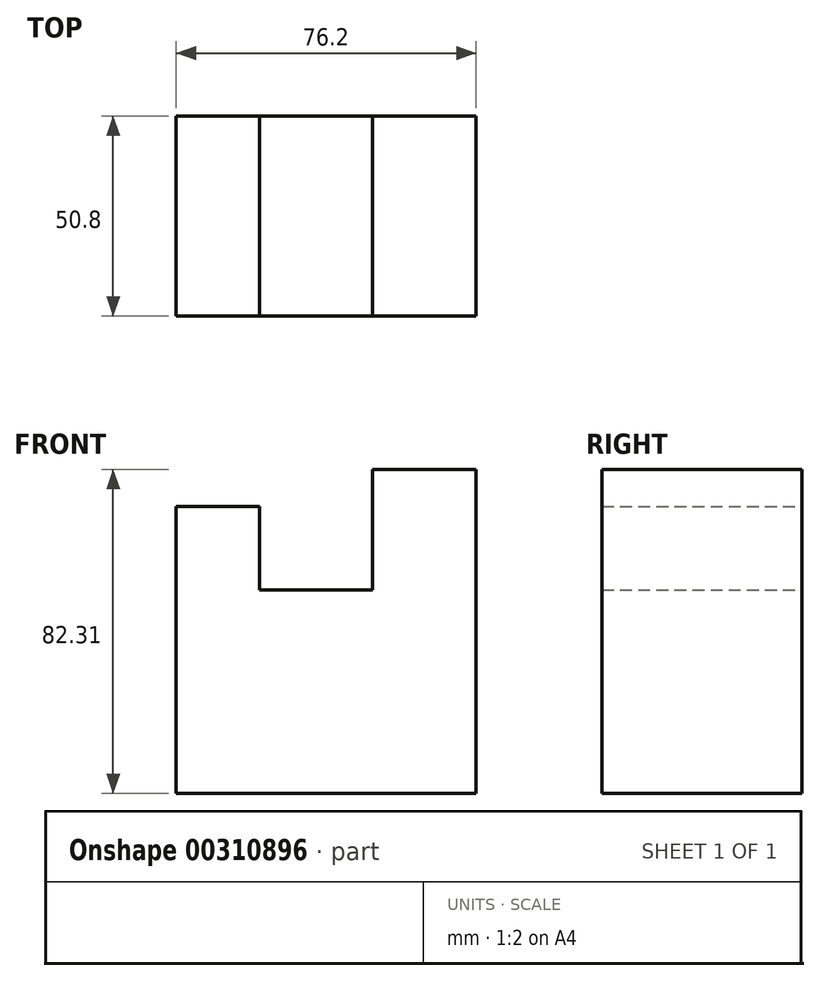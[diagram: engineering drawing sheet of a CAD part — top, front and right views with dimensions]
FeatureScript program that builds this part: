
annotation { "Feature Type Name" : "Feature", "Feature Type Description" : "" }
export const myFeature = defineFeature(function(context is Context, id is Id, definition is map)
    precondition{}
    {
        {
            var Q0;
            Q0=qCreatedBy(makeId("Front.planeOp"),FACE);
            var sketch = newSketch(context, id + "F0", { "sketchPlane" : qUnion([Q0])});
            skLineSegment(sketch, "E0", {"start": v(-55.43, -57.56) * mm, "end": v(20.77, -57.56) * mm});
            skLineSegment(sketch, "E1", {"start": v(20.77, -57.56) * mm, "end": v(20.77, 24.75) * mm});
            skLineSegment(sketch, "E2", {"start": v(-5.57, 24.75) * mm, "end": v(20.77, 24.75) * mm});
            skLineSegment(sketch, "E3", {"start": v(-5.57, 24.75) * mm, "end": v(-5.57, -5.82) * mm});
            skLineSegment(sketch, "E4", {"start": v(-34.27, -5.82) * mm, "end": v(-5.57, -5.82) * mm});
            skLineSegment(sketch, "E5", {"start": v(-34.27, -5.82) * mm, "end": v(-34.27, 15.35) * mm});
            skLineSegment(sketch, "E6", {"start": v(-34.27, 15.35) * mm, "end": v(-55.43, 15.35) * mm});
            skLineSegment(sketch, "E7", {"start": v(-55.43, 15.35) * mm, "end": v(-55.43, -57.56) * mm});
            skSolve(sketch);
        }
        {
            var Q0;
            Q0=makeQuery(id+"F0.imprint","IMPRINT",FACE,{"disambiguationData":[TD([[makeQuery(id+"F0.imprint","IMPRINT",EDGE,{"derivedFrom":sQuery(id+"F0.wireOp",EDGE,"E0")}),1.0]])]});
            extrude(context, id + "F1", {"entities" : qUnion([Q0]), "depth" : 50.8 * mm});
        }
    });
